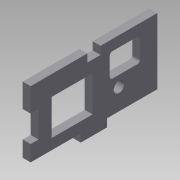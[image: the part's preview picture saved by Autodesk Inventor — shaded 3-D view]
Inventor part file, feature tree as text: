
AUTODESK INVENTOR PART (.ipt)
format: ipt  version: 2013 (Build 170138000, 138)  size: 121,856 bytes
history: native  units: mm
features: extrude x1, sketch x1
ambient origin geometry x8: Origin, YZ Plane, XZ Plane, XY Plane, X Axis, Y Axis, Z Axis, Center Point
feature tree (2):
  extrude  "Extrusion5"  Depth=19.0mm
  sketch  "Sketch1"  dims[d2=3.0mm d4=19.0mm d5=3.0mm d6=3.0mm d7=3.0mm d8=10.0mm d15=3.0mm d16=10.0mm d48=5.0mm d54=21.5mm d61=15.5mm d62=13.5mm d63=4.0mm d66=1.0mm d67=6.5mm d68=4.0mm d69=10.0mm d71=48.0mm d72=25.0mm d73=25.0mm d75=19.0mm d76=4.0mm d77=6.5mm d78=4.0mm d79=5.0mm d80=8.0mm d81=3.0mm d82=0.0mm d85=9.0mm]
